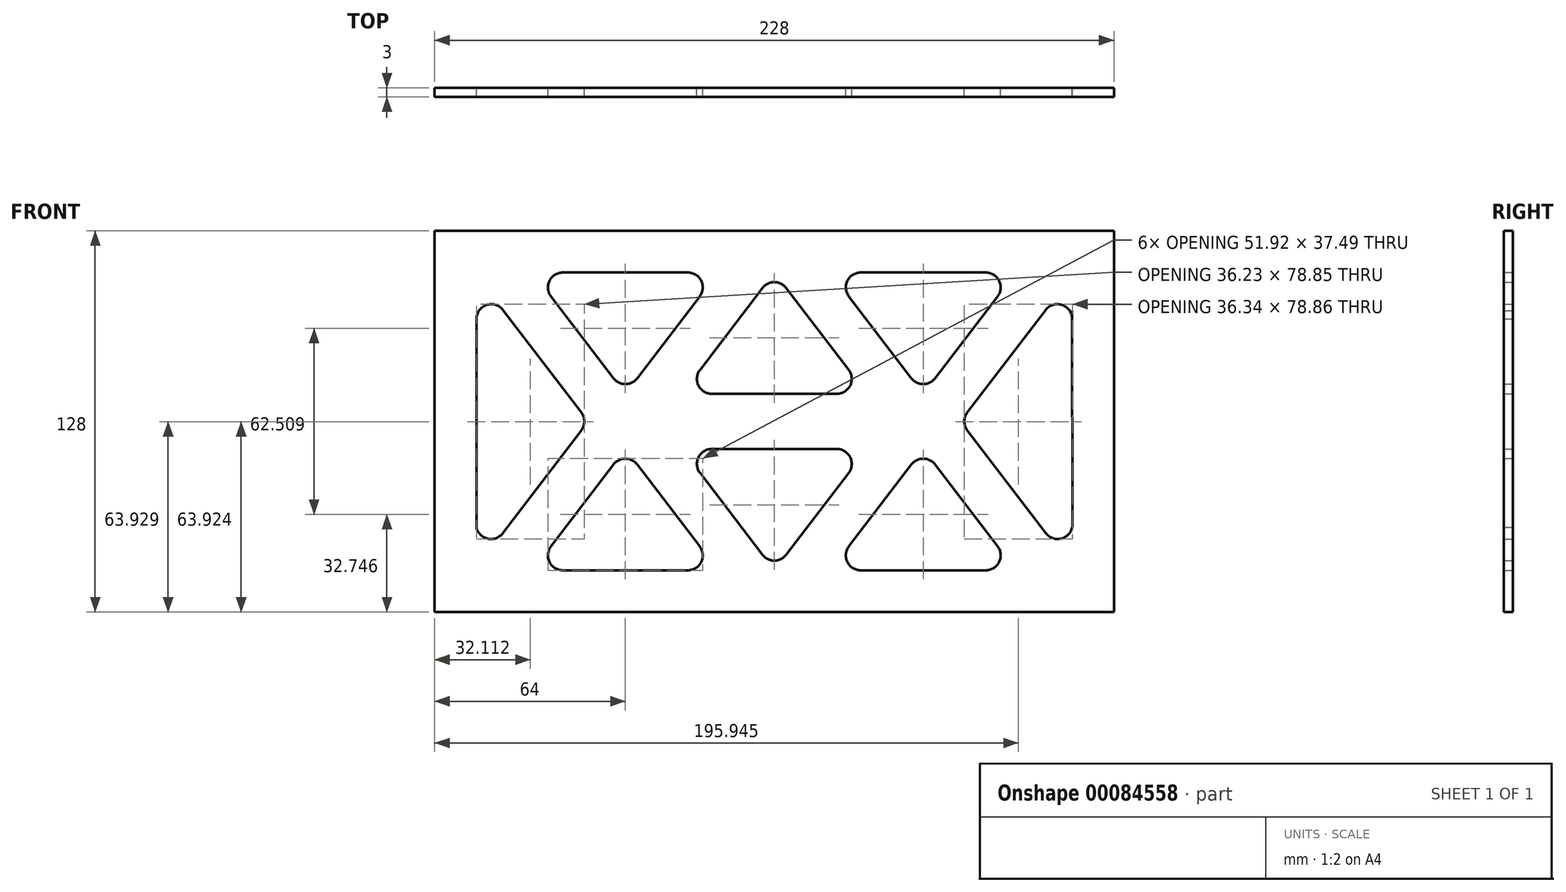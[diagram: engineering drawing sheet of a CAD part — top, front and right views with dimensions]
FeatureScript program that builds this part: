
annotation { "Feature Type Name" : "Feature", "Feature Type Description" : "" }
export const myFeature = defineFeature(function(context is Context, id is Id, definition is map)
    precondition{}
    {
        {
            var Q0;
            Q0=qCreatedBy(makeId("Front.planeOp"),FACE);
            var sketch = newSketch(context, id + "F0", { "sketchPlane" : qUnion([Q0]) });
            skLineSegment(sketch, "E0.bottom", {"start": v(100, -50) * mm, "end": v(-100, -50) * mm});
            skLineSegment(sketch, "E0.top", {"start": v(100, 50) * mm, "end": v(-100, 50) * mm});
            skLineSegment(sketch, "E0.left", {"start": v(100, -50) * mm, "end": v(100, 50) * mm});
            skLineSegment(sketch, "E0.right", {"start": v(-100, -50) * mm, "end": v(-100, 50) * mm});
            skPoint(sketch, "E0.middle", {"position": v(0, 0) * mm});
            skLineSegment(sketch, "E1", {"start": v(0, 50) * mm, "end": v(0, -50) * mm, "construction": true});
            skLineSegment(sketch, "E2", {"start": v(-100, 0) * mm, "end": v(100, 0) * mm, "construction": true});
            skLineSegment(sketch, "E3", {"start": v(29.02, 50) * mm, "end": v(70.98, 50) * mm, "construction": true});
            skLineSegment(sketch, "E4", {"start": v(100, 34.36) * mm, "end": v(100, 0) * mm, "construction": true});
            skLineSegment(sketch, "E5", {"start": v(3.97, 44.8) * mm, "end": v(24.96, 17.3) * mm});
            skLineSegment(sketch, "E6", {"start": v(20.98, 9.27) * mm, "end": v(0, 9.27) * mm});
            skLineSegment(sketch, "E7", {"start": v(46.03, 14.48) * mm, "end": v(25.04, 41.97) * mm});
            skPoint(sketch, "E7.startSnap0", {"position": v(50, 50) * mm});
            skPoint(sketch, "E7.endSnap0", {"position": v(50, 50) * mm});
            skLineSegment(sketch, "E8", {"start": v(50, 50) * mm, "end": v(50, 9.27) * mm, "construction": true});
            skLineSegment(sketch, "E9.MirrorCS", {"start": v(53.97, 14.48) * mm, "end": v(74.96, 41.97) * mm});
            skLineSegment(sketch, "E10", {"start": v(91.03, 37.39) * mm, "end": v(64.8, 3.03) * mm});
            skLineSegment(sketch, "E11.MirrorCS", {"start": v(91.14, -37.54) * mm, "end": v(64.8, -3.03) * mm});
            skLineSegment(sketch, "E12.MirrorCS", {"start": v(53.97, -14.48) * mm, "end": v(74.96, -41.97) * mm});
            skLineSegment(sketch, "E13.MirrorCS", {"start": v(46.03, -14.48) * mm, "end": v(25.04, -41.97) * mm});
            skLineSegment(sketch, "E14.MirrorCS", {"start": v(3.97, -44.8) * mm, "end": v(24.96, -17.3) * mm});
            skLineSegment(sketch, "E15.MirrorCS", {"start": v(20.98, -9.27) * mm, "end": v(0, -9.27) * mm});
            skLineSegment(sketch, "E16", {"start": v(18.41, 50) * mm, "end": v(81.59, 50) * mm});
            skLineSegment(sketch, "E17", {"start": v(100, 37.23) * mm, "end": v(100.12, -34.5) * mm});
            skLineSegment(sketch, "E18", {"start": v(70.98, -50) * mm, "end": v(29.02, -50) * mm});
            skPoint(sketch, "E19.visualSharp", {"position": v(50, 9.27) * mm});
            skArc(sketch, "E19.filletArc", {"start": v(46.03, 14.48) * mm, "mid": v(50, 12.5) * mm, "end": v(53.97, 14.48) * mm});
            skPoint(sketch, "E20.visualSharp", {"position": v(31.1, 9.27) * mm});
            skArc(sketch, "E20.filletArc", {"start": v(20.98, 9.27) * mm, "mid": v(25.47, 12.05) * mm, "end": v(24.96, 17.3) * mm});
            skPoint(sketch, "E21.visualSharp", {"position": v(31.1, -9.27) * mm});
            skArc(sketch, "E21.filletArc", {"start": v(24.96, -17.3) * mm, "mid": v(25.47, -12.05) * mm, "end": v(20.98, -9.27) * mm});
            skPoint(sketch, "E22.visualSharp", {"position": v(50, -9.27) * mm});
            skArc(sketch, "E22.filletArc", {"start": v(53.97, -14.48) * mm, "mid": v(50, -12.5) * mm, "end": v(46.03, -14.48) * mm});
            skPoint(sketch, "E23.visualSharp", {"position": v(62.48, 0) * mm});
            skArc(sketch, "E23.filletArc", {"start": v(64.8, 3.03) * mm, "mid": v(63.78, 0) * mm, "end": v(64.8, -3.03) * mm});
            skPoint(sketch, "E24.newPointA", {"position": v(100.14, 49.33) * mm});
            skArc(sketch, "E24.filletArc", {"start": v(100, 34.36) * mm, "mid": v(96.6, 39.1) * mm, "end": v(91.03, 37.39) * mm});
            skPoint(sketch, "E25.newPointA", {"position": v(81.1, 50) * mm});
            skPoint(sketch, "E25.newPointB", {"position": v(100, 50) * mm});
            skArc(sketch, "E25.filletArc", {"start": v(74.96, 41.97) * mm, "mid": v(75.47, 47.22) * mm, "end": v(70.98, 50) * mm});
            skPoint(sketch, "E26.newPointA", {"position": v(18.9, 50) * mm});
            skPoint(sketch, "E26.newPointB", {"position": v(0, 50) * mm});
            skArc(sketch, "E26.filletArc", {"start": v(29.02, 50) * mm, "mid": v(24.53, 47.22) * mm, "end": v(25.04, 41.97) * mm});
            skPoint(sketch, "E27.visualSharp", {"position": v(100.14, -49.33) * mm});
            skArc(sketch, "E27.filletArc", {"start": v(91.14, -37.54) * mm, "mid": v(96.72, -39.24) * mm, "end": v(100.12, -34.5) * mm});
            skPoint(sketch, "E28.visualSharp", {"position": v(81.1, -50) * mm});
            skArc(sketch, "E28.filletArc", {"start": v(70.98, -50) * mm, "mid": v(75.47, -47.22) * mm, "end": v(74.96, -41.97) * mm});
            skPoint(sketch, "E29.visualSharp", {"position": v(18.9, -50) * mm});
            skArc(sketch, "E29.filletArc", {"start": v(25.04, -41.97) * mm, "mid": v(24.53, -47.22) * mm, "end": v(29.02, -50) * mm});
            skLineSegment(sketch, "E30.MirrorCS", {"start": v(-3.97, 44.8) * mm, "end": v(-24.96, 17.3) * mm});
            skLineSegment(sketch, "E31.MirrorCS", {"start": v(-20.98, 9.27) * mm, "end": v(0, 9.27) * mm});
            skArc(sketch, "E32.MirrorCS", {"start": v(-20.98, 9.27) * mm, "mid": v(-25.47, 12.05) * mm, "end": v(-24.96, 17.3) * mm});
            skLineSegment(sketch, "E33.MirrorCS", {"start": v(-46.03, 14.48) * mm, "end": v(-25.04, 41.97) * mm});
            skArc(sketch, "E34.MirrorCS", {"start": v(-29.02, 50) * mm, "mid": v(-24.53, 47.22) * mm, "end": v(-25.04, 41.97) * mm});
            skArc(sketch, "E35.MirrorCS", {"start": v(-46.03, 14.48) * mm, "mid": v(-50, 12.5) * mm, "end": v(-53.97, 14.48) * mm});
            skLineSegment(sketch, "E36.MirrorCS", {"start": v(-53.97, 14.48) * mm, "end": v(-74.96, 41.97) * mm});
            skArc(sketch, "E37.MirrorCS", {"start": v(-74.96, 41.97) * mm, "mid": v(-75.47, 47.22) * mm, "end": v(-70.98, 50) * mm});
            skLineSegment(sketch, "E38.MirrorCS", {"start": v(-91.03, 37.39) * mm, "end": v(-64.8, 3.03) * mm});
            skLineSegment(sketch, "E39.MirrorCS", {"start": v(-91.14, -37.54) * mm, "end": v(-64.8, -3.03) * mm});
            skArc(sketch, "E40.MirrorCS", {"start": v(-91.14, -37.54) * mm, "mid": v(-96.72, -39.24) * mm, "end": v(-100.12, -34.5) * mm});
            skArc(sketch, "E41.MirrorCS", {"start": v(-100, 34.36) * mm, "mid": v(-96.6, 39.1) * mm, "end": v(-91.03, 37.39) * mm});
            skArc(sketch, "E42.MirrorCS", {"start": v(-53.97, -14.48) * mm, "mid": v(-50, -12.5) * mm, "end": v(-46.03, -14.48) * mm});
            skLineSegment(sketch, "E43.MirrorCS", {"start": v(-53.97, -14.48) * mm, "end": v(-74.96, -41.97) * mm});
            skLineSegment(sketch, "E44.MirrorCS", {"start": v(-46.03, -14.48) * mm, "end": v(-25.04, -41.97) * mm});
            skArc(sketch, "E45.MirrorCS", {"start": v(-25.04, -41.97) * mm, "mid": v(-24.53, -47.22) * mm, "end": v(-29.02, -50) * mm});
            skArc(sketch, "E46.MirrorCS", {"start": v(-70.98, -50) * mm, "mid": v(-75.47, -47.22) * mm, "end": v(-74.96, -41.97) * mm});
            skLineSegment(sketch, "E47.MirrorCS", {"start": v(-20.98, -9.27) * mm, "end": v(0, -9.27) * mm});
            skLineSegment(sketch, "E48.MirrorCS", {"start": v(-3.97, -44.8) * mm, "end": v(-24.96, -17.3) * mm});
            skArc(sketch, "E49.MirrorCS", {"start": v(-24.96, -17.3) * mm, "mid": v(-25.47, -12.05) * mm, "end": v(-20.98, -9.27) * mm});
            skArc(sketch, "E50.MirrorCS", {"start": v(-64.8, 3.03) * mm, "mid": v(-63.78, 0) * mm, "end": v(-64.8, -3.03) * mm});
            skLineSegment(sketch, "E51.0", {"start": v(114, 64) * mm, "end": v(-114, 64) * mm});
            skLineSegment(sketch, "E51.1", {"start": v(114, -64) * mm, "end": v(114, 64) * mm});
            skLineSegment(sketch, "E51.2", {"start": v(114, -64) * mm, "end": v(-114, -64) * mm});
            skLineSegment(sketch, "E51.3", {"start": v(-114, -64) * mm, "end": v(-114, 64) * mm});
            skArc(sketch, "E52.filletArc", {"start": v(3.97, 44.8) * mm, "mid": v(0, 46.76) * mm, "end": v(-3.97, 44.8) * mm});
            skPoint(sketch, "E53.visualSharp", {"position": v(0, -50) * mm});
            skArc(sketch, "E53.filletArc", {"start": v(-3.97, -44.8) * mm, "mid": v(0, -46.76) * mm, "end": v(3.97, -44.8) * mm});
            skSolve(sketch);
        }
        {
            var Q0;
            {var subQ20=sQuery(id+"F0.wireOp",EDGE,"E18");Q0=makeQuery(id+"F0.imprint","IMPRINT",FACE,{"disambiguationData":[TD([[makeQuery(id+"F0.imprint","IMPRINT",EDGE,{"derivedFrom":subQ20}),1.0]])]});}
            var Q1;
            {var subQ20=sQuery(id+"F0.wireOp",EDGE,"E5");Q1=makeQuery(id+"F0.imprint","IMPRINT",FACE,{"disambiguationData":[TD([[makeQuery(id+"F0.imprint","IMPRINT",EDGE,{"derivedFrom":subQ20}),1.0]])]});}
            extrude(context, id + "F1", {"entities" : qUnion([Q0, Q1]), "depth" : 3 * mm});
        }
    });
